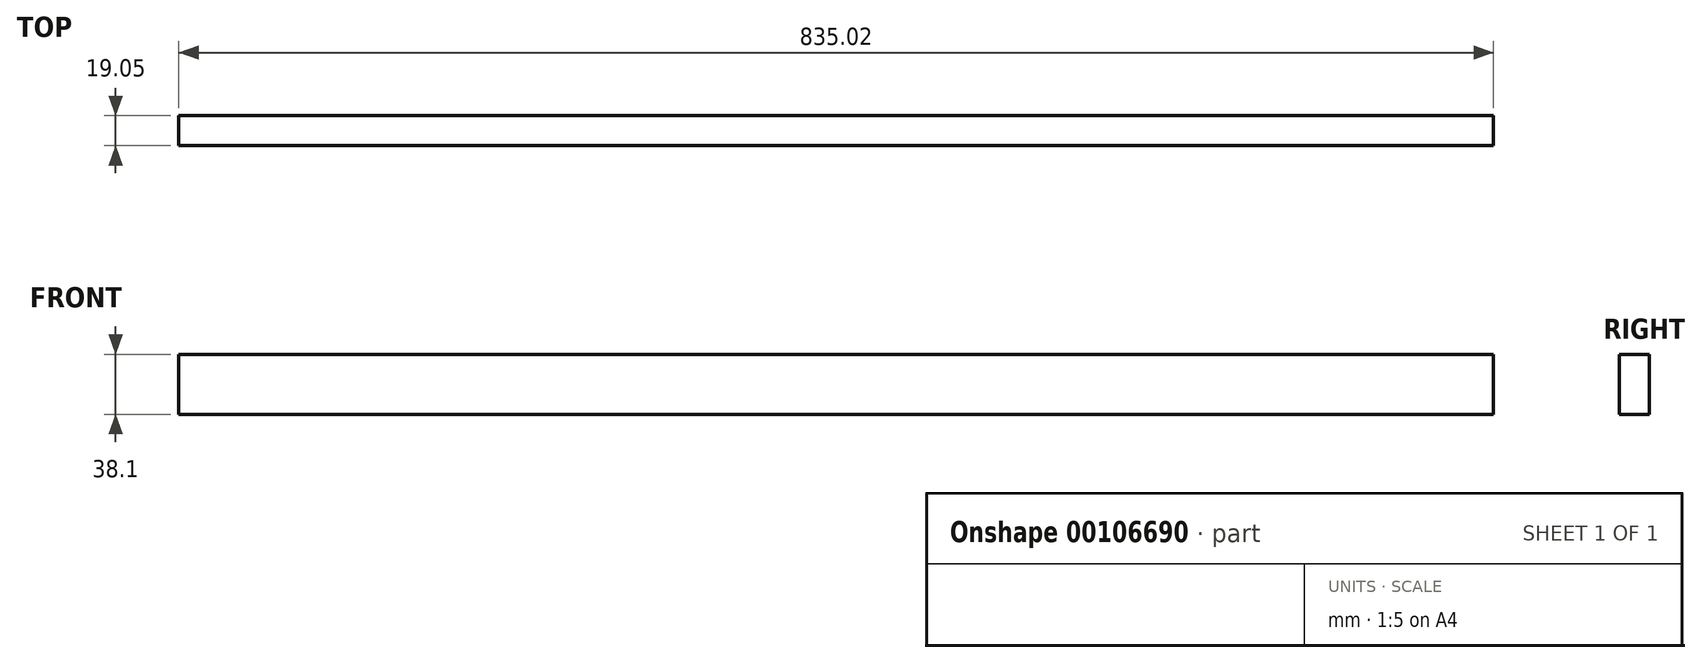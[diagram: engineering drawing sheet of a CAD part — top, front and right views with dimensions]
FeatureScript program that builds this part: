
annotation { "Feature Type Name" : "Feature", "Feature Type Description" : "" }
export const myFeature = defineFeature(function(context is Context, id is Id, definition is map)
    precondition{}
    {
        {
            var Q0;
            Q0=qCreatedBy(makeId("Front.planeOp"),FACE);
            var sketch = newSketch(context, id + "F0", { "sketchPlane" : qUnion([Q0])});
            skLineSegment(sketch, "E0.bottom", {"start": v(0, 0) * mm, "end": v(835.03, 0) * mm});
            skLineSegment(sketch, "E0.top", {"start": v(0, 38.1) * mm, "end": v(835.03, 38.1) * mm});
            skLineSegment(sketch, "E0.left", {"start": v(0, 0) * mm, "end": v(0, 38.1) * mm});
            skLineSegment(sketch, "E0.right", {"start": v(835.03, 0) * mm, "end": v(835.03, 38.1) * mm});
            skSolve(sketch);
        }
        {
            var Q0;
            Q0=makeQuery(id+"F0.imprint","IMPRINT",FACE,{"disambiguationData":[TD([[makeQuery(id+"F0.imprint","IMPRINT",EDGE,{"derivedFrom":sQuery(id+"F0.wireOp",EDGE,"E0.bottom")}),1.0]])]});
            extrude(context, id + "F1", {"entities" : qUnion([Q0]), "depth" : 19.05 * mm});
        }
    });
